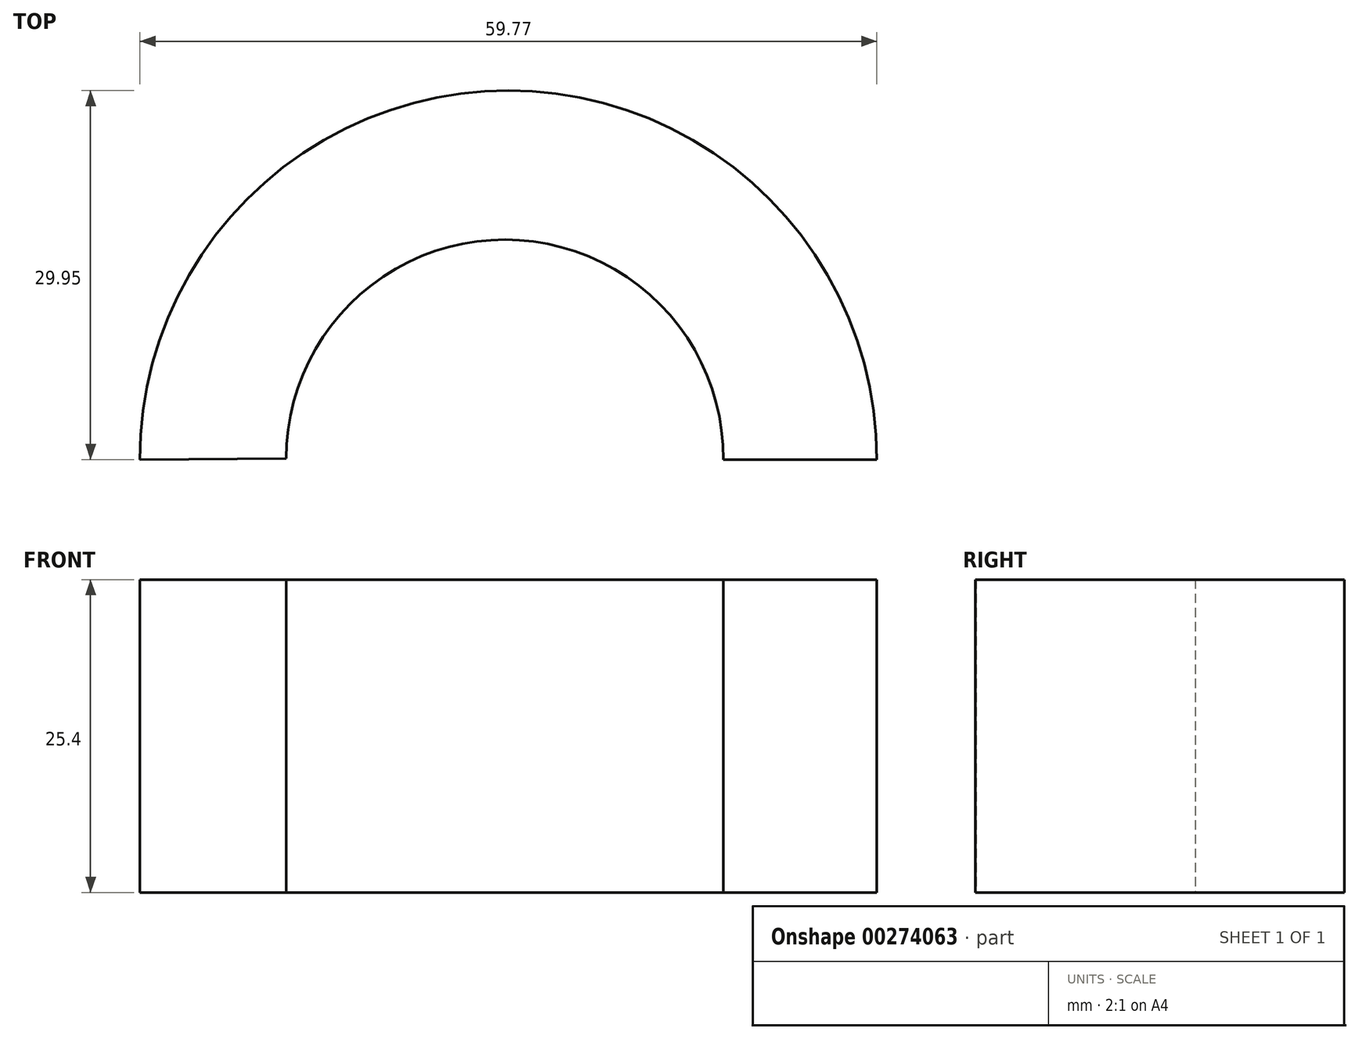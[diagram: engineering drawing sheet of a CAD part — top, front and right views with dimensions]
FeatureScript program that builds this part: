
annotation { "Feature Type Name" : "Feature", "Feature Type Description" : "" }
export const myFeature = defineFeature(function(context is Context, id is Id, definition is map)
    precondition{}
    {
        {
            var Q0;
            Q0=qCreatedBy(makeId("Top.planeOp"),FACE);
            var sketch = newSketch(context, id + "F0", { "sketchPlane" : qUnion([Q0])});
            skArc(sketch, "E0", {"start": v(29.33, 0) * mm, "mid": v(-0.56, 29.95) * mm, "end": v(-30.44, 0) * mm});
            skLineSegment(sketch, "E1", {"start": v(-30.44, 0) * mm, "end": v(-18.57, 0.07) * mm});
            skLineSegment(sketch, "E2", {"start": v(29.33, 0) * mm, "end": v(16.89, 0) * mm});
            skArc(sketch, "E3", {"start": v(16.89, 0) * mm, "mid": v(-0.8, 17.85) * mm, "end": v(-18.57, 0.07) * mm});
            skSolve(sketch);
        }
        {
            var Q0;
            Q0 = qSketchRegion(id + "F0", true);
            extrude(context, id + "F1", {"entities" : qUnion([Q0]), "depth" : 25.4 * mm});
        }
    });
